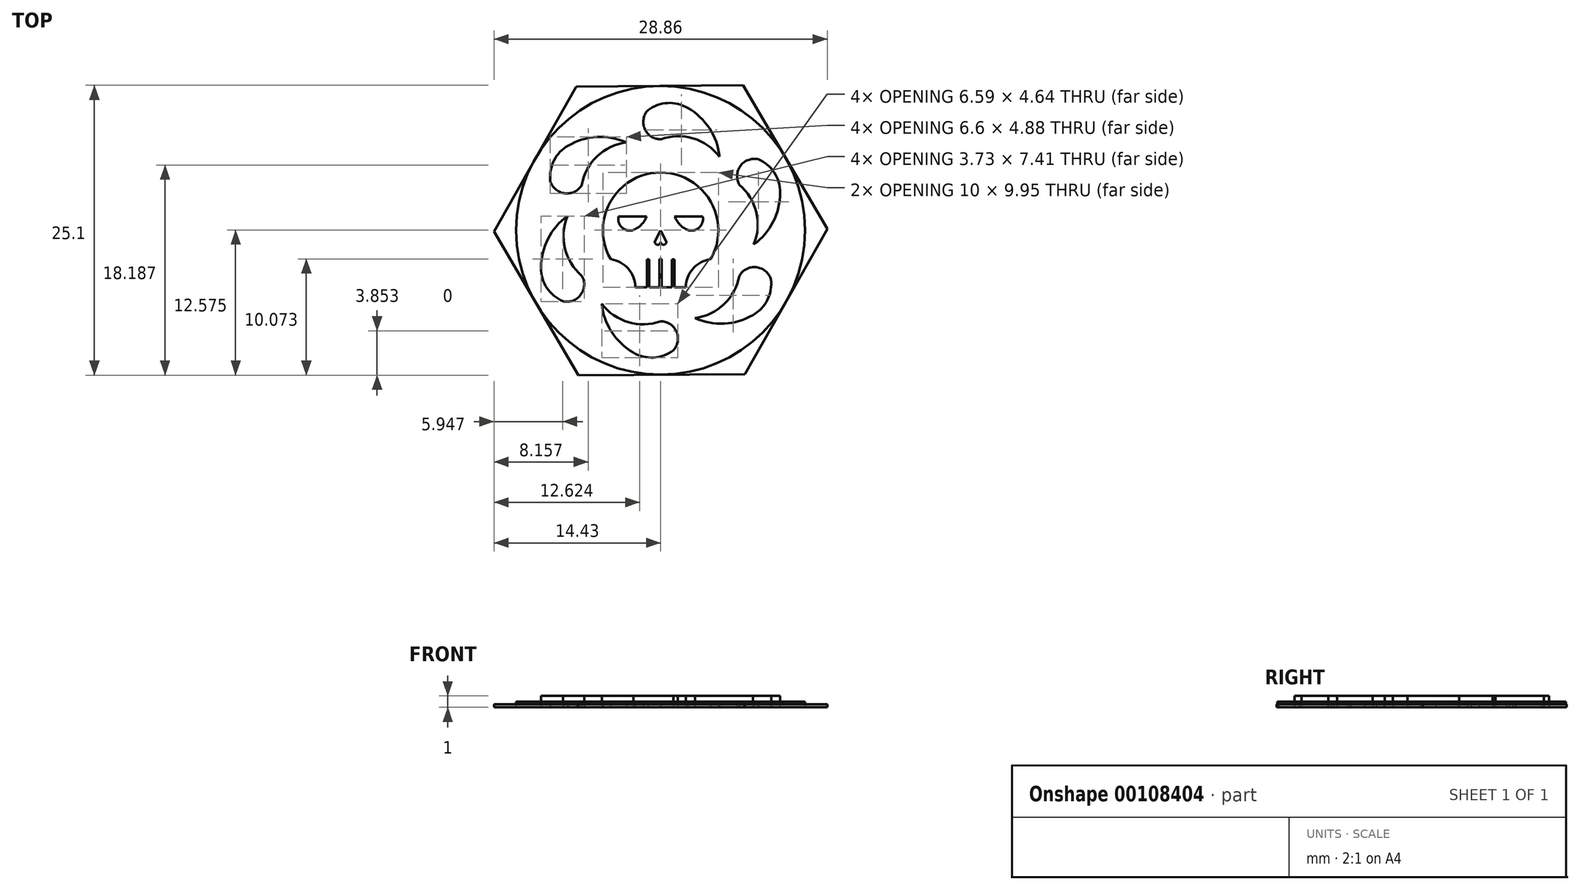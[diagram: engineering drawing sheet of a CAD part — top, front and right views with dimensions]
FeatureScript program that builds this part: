
annotation { "Feature Type Name" : "Feature", "Feature Type Description" : "" }
export const myFeature = defineFeature(function(context is Context, id is Id, definition is map)
    precondition{}
    {
        {
            var Q0;
            Q0=qCreatedBy(makeId("Top.planeOp"),FACE);
            var sketch = newSketch(context, id + "F0", { "sketchPlane" : qUnion([Q0])});
            skArc(sketch, "E0", {"start": v(4.33, -2.5) * mm, "mid": v(0, 5) * mm, "end": v(-4.33, -2.5) * mm});
            skLineSegment(sketch, "E1", {"start": v(0, -1) * mm, "end": v(0, -2.5) * mm});
            skArc(sketch, "E2", {"start": v(-2.19, -4.95) * mm, "mid": v(-2.8, -3.33) * mm, "end": v(-4.33, -2.5) * mm});
            skArc(sketch, "E3", {"start": v(4.33, -2.5) * mm, "mid": v(2.8, -3.33) * mm, "end": v(2.19, -4.95) * mm});
            skLineSegment(sketch, "E4", {"start": v(2.19, -4.95) * mm, "end": v(-2.19, -4.95) * mm});
            skPoint(sketch, "E5.start.orphan", {"position": v(0, -2.5) * mm});
            skLineSegment(sketch, "E6", {"start": v(0, 0) * mm, "end": v(0, 1.2) * mm});
            skLineSegment(sketch, "E7", {"start": v(-1.21, 1.2) * mm, "end": v(-3.64, 1.2) * mm});
            skLineSegment(sketch, "E8", {"start": v(1.21, 1.2) * mm, "end": v(3.64, 1.2) * mm});
            skLineSegment(sketch, "E9", {"start": v(-2.43, 1.2) * mm, "end": v(-3.64, 1.2) * mm});
            skLineSegment(sketch, "E10", {"start": v(-2.43, 1.2) * mm, "end": v(-1.21, 1.2) * mm});
            skLineSegment(sketch, "E11", {"start": v(1.21, 1.2) * mm, "end": v(2.43, 1.2) * mm});
            skLineSegment(sketch, "E12", {"start": v(2.43, 1.2) * mm, "end": v(3.64, 1.2) * mm});
            skArc(sketch, "E13", {"start": v(-3.64, 1.2) * mm, "mid": v(-3.37, 0.26) * mm, "end": v(-2.43, 0) * mm});
            skArc(sketch, "E14", {"start": v(-2.43, 0) * mm, "mid": v(-1.69, 0.46) * mm, "end": v(-1.21, 1.2) * mm});
            skArc(sketch, "E15", {"start": v(1.21, 1.2) * mm, "mid": v(1.69, 0.46) * mm, "end": v(2.43, 0) * mm});
            skArc(sketch, "E16", {"start": v(2.43, 0) * mm, "mid": v(3.37, 0.26) * mm, "end": v(3.64, 1.2) * mm});
            skPoint(sketch, "E17.orphan", {"position": v(-4.85, 1.2) * mm});
            skPoint(sketch, "E18.orphan", {"position": v(4.85, 1.2) * mm});
            skLineSegment(sketch, "E19", {"start": v(0, -1) * mm, "end": v(0, -1.5) * mm});
            skLineSegment(sketch, "E20", {"start": v(-0.5, -1) * mm, "end": v(0, 0) * mm});
            skLineSegment(sketch, "E21", {"start": v(0, 0) * mm, "end": v(0.5, -1) * mm});
            skArc(sketch, "E22", {"start": v(-0.5, -1) * mm, "mid": v(-0.25, -1.25) * mm, "end": v(0, -1) * mm});
            skArc(sketch, "E23", {"start": v(0, -1) * mm, "mid": v(0.25, -1.25) * mm, "end": v(0.5, -1) * mm});
            skPoint(sketch, "E23.midSnap0", {"position": v(0.25, -1) * mm});
            skPoint(sketch, "E23.midSnap1", {"position": v(0, -1.25) * mm});
            skLineSegment(sketch, "E24", {"start": v(0, -4.95) * mm, "end": v(-2.19, -4.95) * mm});
            skLineSegment(sketch, "E25", {"start": v(0, -4.95) * mm, "end": v(2.19, -4.95) * mm});
            skLineSegment(sketch, "E26", {"start": v(-0.1, -4.78) * mm, "end": v(-0.1, -4.95) * mm});
            skLineSegment(sketch, "E27", {"start": v(0.1, -4.78) * mm, "end": v(0.1, -4.95) * mm});
            skLineSegment(sketch, "E28", {"start": v(-1.2, -4.81) * mm, "end": v(-1.2, -4.95) * mm});
            skLineSegment(sketch, "E29", {"start": v(-1, -4.81) * mm, "end": v(-1, -4.95) * mm});
            skLineSegment(sketch, "E30", {"start": v(1, -4.81) * mm, "end": v(1, -4.95) * mm});
            skLineSegment(sketch, "E31", {"start": v(1.2, -4.81) * mm, "end": v(1.2, -4.95) * mm});
            skLineSegment(sketch, "E32", {"start": v(0.1, -4.78) * mm, "end": v(0.1, -2.5) * mm});
            skLineSegment(sketch, "E33", {"start": v(-0.1, -4.78) * mm, "end": v(-0.1, -2.5) * mm});
            skLineSegment(sketch, "E34", {"start": v(-1, -4.81) * mm, "end": v(-1, -2.53) * mm});
            skLineSegment(sketch, "E35", {"start": v(-1.2, -4.81) * mm, "end": v(-1.2, -2.53) * mm});
            skLineSegment(sketch, "E36", {"start": v(1, -4.81) * mm, "end": v(1, -2.53) * mm});
            skLineSegment(sketch, "E37", {"start": v(1.2, -4.81) * mm, "end": v(1.2, -2.53) * mm});
            skLineSegment(sketch, "E38", {"start": v(-1.2, -2.53) * mm, "end": v(-1, -2.53) * mm});
            skLineSegment(sketch, "E39", {"start": v(-0.1, -2.5) * mm, "end": v(0.1, -2.5) * mm});
            skLineSegment(sketch, "E40", {"start": v(1, -2.53) * mm, "end": v(1.2, -2.53) * mm});
            skCircle(sketch, "E41", {"center": v(0, 0) * mm, "radius": 12.5 * mm});
            skLineSegment(sketch, "E42", {"start": v(0, 0) * mm, "end": v(0, 12.5) * mm});
            skLineSegment(sketch, "E43", {"start": v(0, 6.25) * mm, "end": v(0, 12.5) * mm});
            skArc(sketch, "E44", {"start": v(5.1, 6.38) * mm, "mid": v(2.8, 7.96) * mm, "end": v(0, 7.87) * mm});
            skArc(sketch, "E45", {"start": v(2.35, 10.59) * mm, "mid": v(0.6, 11.02) * mm, "end": v(-1.1, 10.4) * mm});
            skArc(sketch, "E46.trimOffspring", {"start": v(-1.1, 10.4) * mm, "mid": v(-1.38, 8.78) * mm, "end": v(0, 7.87) * mm});
            skPoint(sketch, "E47.center.orphan", {"position": v(0, 9.38) * mm});
            skArc(sketch, "E48", {"start": v(5.1, 6.38) * mm, "mid": v(4.24, 8.81) * mm, "end": v(2.35, 10.59) * mm});
            skArc(sketch, "E49.1.0", {"start": v(-2.97, 7.6) * mm, "mid": v(-5.52, 8.08) * mm, "end": v(-8, 7.33) * mm});
            skArc(sketch, "E49.1.1", {"start": v(-8, 7.33) * mm, "mid": v(-9.24, 6.03) * mm, "end": v(-9.55, 4.25) * mm});
            skArc(sketch, "E49.1.2", {"start": v(-9.55, 4.25) * mm, "mid": v(-8.29, 3.2) * mm, "end": v(-6.82, 3.94) * mm});
            skArc(sketch, "E49.1.3", {"start": v(-2.97, 7.6) * mm, "mid": v(-5.5, 6.4) * mm, "end": v(-6.82, 3.94) * mm});
            skArc(sketch, "E49.2.0", {"start": v(-8.07, 1.23) * mm, "mid": v(-9.75, -0.74) * mm, "end": v(-10.35, -3.26) * mm});
            skArc(sketch, "E49.2.1", {"start": v(-10.35, -3.26) * mm, "mid": v(-9.84, -4.99) * mm, "end": v(-8.46, -6.15) * mm});
            skArc(sketch, "E49.2.2", {"start": v(-8.46, -6.15) * mm, "mid": v(-6.91, -5.58) * mm, "end": v(-6.82, -3.94) * mm});
            skArc(sketch, "E49.2.3", {"start": v(-8.07, 1.23) * mm, "mid": v(-8.29, -1.56) * mm, "end": v(-6.82, -3.94) * mm});
            skArc(sketch, "E49.3.0", {"start": v(-5.1, -6.38) * mm, "mid": v(-4.24, -8.81) * mm, "end": v(-2.35, -10.59) * mm});
            skArc(sketch, "E49.3.1", {"start": v(-2.35, -10.59) * mm, "mid": v(-0.6, -11.02) * mm, "end": v(1.1, -10.4) * mm});
            skArc(sketch, "E49.3.2", {"start": v(1.1, -10.4) * mm, "mid": v(1.38, -8.78) * mm, "end": v(0, -7.87) * mm});
            skArc(sketch, "E49.3.3", {"start": v(-5.1, -6.38) * mm, "mid": v(-2.8, -7.96) * mm, "end": v(0, -7.87) * mm});
            skArc(sketch, "E49.4.0", {"start": v(2.97, -7.6) * mm, "mid": v(5.52, -8.08) * mm, "end": v(8, -7.33) * mm});
            skArc(sketch, "E49.4.1", {"start": v(8, -7.33) * mm, "mid": v(9.24, -6.03) * mm, "end": v(9.55, -4.25) * mm});
            skArc(sketch, "E49.4.2", {"start": v(9.55, -4.25) * mm, "mid": v(8.29, -3.2) * mm, "end": v(6.82, -3.94) * mm});
            skArc(sketch, "E49.4.3", {"start": v(2.97, -7.6) * mm, "mid": v(5.5, -6.4) * mm, "end": v(6.82, -3.94) * mm});
            skArc(sketch, "E49.5.0", {"start": v(8.07, -1.23) * mm, "mid": v(9.75, 0.74) * mm, "end": v(10.35, 3.26) * mm});
            skArc(sketch, "E49.5.1", {"start": v(10.35, 3.26) * mm, "mid": v(9.84, 4.99) * mm, "end": v(8.46, 6.15) * mm});
            skArc(sketch, "E49.5.2", {"start": v(8.46, 6.15) * mm, "mid": v(6.91, 5.58) * mm, "end": v(6.82, 3.94) * mm});
            skArc(sketch, "E49.5.3", {"start": v(8.07, -1.23) * mm, "mid": v(8.29, 1.56) * mm, "end": v(6.82, 3.94) * mm});
            skCircle(sketch, "E50.cCircle", {"center": v(0, 0) * mm, "radius": 12.5 * mm, "construction": true});
            skLineSegment(sketch, "E50.0", {"start": v(-14.43, -0.1) * mm, "end": v(-7.3, 12.45) * mm});
            skLineSegment(sketch, "E50.1", {"start": v(-7.3, 12.45) * mm, "end": v(7.13, 12.55) * mm});
            skLineSegment(sketch, "E50.2", {"start": v(7.13, 12.55) * mm, "end": v(14.43, 0.1) * mm});
            skLineSegment(sketch, "E50.3", {"start": v(14.43, 0.1) * mm, "end": v(7.3, -12.45) * mm});
            skLineSegment(sketch, "E50.4", {"start": v(7.3, -12.45) * mm, "end": v(-7.13, -12.55) * mm});
            skLineSegment(sketch, "E50.5", {"start": v(-7.13, -12.55) * mm, "end": v(-14.43, -0.1) * mm});
            skPoint(sketch, "E50.0.midPoint", {"position": v(-10.87, 6.17) * mm});
            skSolve(sketch);
        }
        {
            var Q0;
            {var subQ0=sQuery(id+"F0.wireOp",EDGE,"E44");Q0=makeQuery(id+"F0.imprint","IMPRINT",FACE,{"disambiguationData":[TD([[makeQuery(id+"F0.imprint","IMPRINT",EDGE,{"derivedFrom":subQ0}),-1.0]])]});}
            var Q1;
            {var subQ0=sQuery(id+"F0.wireOp",EDGE,"E46.trimOffspring");Q1=makeQuery(id+"F0.imprint","IMPRINT",FACE,{"disambiguationData":[TD([[makeQuery(id+"F0.imprint","IMPRINT",EDGE,{"derivedFrom":subQ0}),1.0]])]});}
            var Q2;
            Q2=makeQuery(id+"F0.imprint","IMPRINT",FACE,{"disambiguationData":[TD([[makeQuery(id+"F0.imprint","IMPRINT",EDGE,{"derivedFrom":sQuery(id+"F0.wireOp",EDGE,"E49.1.0")}),1.0]])]});
            var Q3;
            Q3=makeQuery(id+"F0.imprint","IMPRINT",FACE,{"disambiguationData":[TD([[makeQuery(id+"F0.imprint","IMPRINT",EDGE,{"derivedFrom":sQuery(id+"F0.wireOp",EDGE,"E49.2.0")}),1.0]])]});
            var Q4;
            Q4=makeQuery(id+"F0.imprint","IMPRINT",FACE,{"disambiguationData":[TD([[makeQuery(id+"F0.imprint","IMPRINT",EDGE,{"derivedFrom":sQuery(id+"F0.wireOp",EDGE,"E49.3.0")}),1.0]])]});
            var Q5;
            Q5=makeQuery(id+"F0.imprint","IMPRINT",FACE,{"disambiguationData":[TD([[makeQuery(id+"F0.imprint","IMPRINT",EDGE,{"derivedFrom":sQuery(id+"F0.wireOp",EDGE,"E49.4.0")}),1.0]])]});
            var Q6;
            Q6=makeQuery(id+"F0.imprint","IMPRINT",FACE,{"disambiguationData":[TD([[makeQuery(id+"F0.imprint","IMPRINT",EDGE,{"derivedFrom":sQuery(id+"F0.wireOp",EDGE,"E49.5.0")}),1.0]])]});
            var Q7;
            {var subQ6=sQuery(id+"F0.wireOp",EDGE,"E1");Q7=makeQuery(id+"F0.imprint","IMPRINT",FACE,{"disambiguationData":[TD([[makeQuery(id+"F0.imprint","IMPRINT",EDGE,{"derivedFrom":subQ6}),1.0]])]});}
            var Q8;
            {var subQ7=sQuery(id+"F0.wireOp",EDGE,"E1");Q8=makeQuery(id+"F0.imprint","IMPRINT",FACE,{"disambiguationData":[TD([[makeQuery(id+"F0.imprint","IMPRINT",EDGE,{"derivedFrom":subQ7}),-1.0]])]});}
            extrude(context, id + "F1", {"entities" : qUnion([Q0, Q1, Q2, Q3, Q4, Q5, Q6, Q7, Q8]), "depth" : 1 * mm});
        }
        {
            var Q0;
            {var subQ8=sQuery(id+"F0.wireOp",EDGE,"E2");Q0=makeQuery(id+"F0.imprint","IMPRINT",FACE,{"disambiguationData":[TD([[makeQuery(id+"F0.imprint","IMPRINT",EDGE,{"derivedFrom":subQ8}),1.0]])]});}
            var Q1;
            Q1=makeQuery(id+"F0.imprint","IMPRINT",FACE,{"disambiguationData":[TD([[makeQuery(id+"F0.imprint","IMPRINT",EDGE,{"derivedFrom":sQuery(id+"F0.wireOp",EDGE,"E9")}),1.0]])]});
            var Q2;
            Q2=makeQuery(id+"F0.imprint","IMPRINT",FACE,{"disambiguationData":[TD([[makeQuery(id+"F0.imprint","IMPRINT",EDGE,{"derivedFrom":sQuery(id+"F0.wireOp",EDGE,"E11")}),-1.0]])]});
            var Q3;
            Q3=makeQuery(id+"F0.imprint","IMPRINT",FACE,{"disambiguationData":[TD([[makeQuery(id+"F0.imprint","IMPRINT",EDGE,{"derivedFrom":sQuery(id+"F0.wireOp",EDGE,"E20")}),-1.0]])]});
            var Q4;
            {var subQ1=sQuery(id+"F0.wireOp",EDGE,"E28");Q4=makeQuery(id+"F0.imprint","IMPRINT",FACE,{"disambiguationData":[TD([[makeQuery(id+"F0.imprint","IMPRINT",EDGE,{"derivedFrom":subQ1}),1.0]])]});}
            var Q5;
            {var subQ1=sQuery(id+"F0.wireOp",EDGE,"E26");Q5=makeQuery(id+"F0.imprint","IMPRINT",FACE,{"disambiguationData":[TD([[makeQuery(id+"F0.imprint","IMPRINT",EDGE,{"derivedFrom":subQ1}),1.0]])]});}
            var Q6;
            {var subQ1=sQuery(id+"F0.wireOp",EDGE,"E30");Q6=makeQuery(id+"F0.imprint","IMPRINT",FACE,{"disambiguationData":[TD([[makeQuery(id+"F0.imprint","IMPRINT",EDGE,{"derivedFrom":subQ1}),1.0]])]});}
            extrude(context, id + "F2", {"entities" : qUnion([Q0, Q1, Q2, Q3, Q4, Q5, Q6]), "depth" : .5 * mm});
        }
        {
            var Q0;
            {var subQ0=sQuery(id+"F0.wireOp",EDGE,"E41");var subQ1=makeQuery(id+"F0.imprint","IMPRINT",VERTEX,{"derivedFrom":subQ0});Q0=makeQuery(id+"F0.imprint","IMPRINT",FACE,{"disambiguationData":[TD([[makeQuery(id+"F0.imprint","IMPRINT",EDGE,{"disambiguationData":[TD([[subQ1,1.0]])],"derivedFrom":subQ0}),-1.0]])]});}
            var Q1;
            {var subQ0=sQuery(id+"F0.wireOp",EDGE,"E50.1");var subQ1=sQuery(id+"F0.wireOp",EDGE,"E41");var subQ2=makeQuery(id+"F0.imprint","INTERSECT",VERTEX,{"derivedFrom":[subQ1,subQ0]});Q1=makeQuery(id+"F0.imprint","IMPRINT",FACE,{"disambiguationData":[TD([[makeQuery(id+"F0.imprint","IMPRINT",EDGE,{"disambiguationData":[TD([[subQ2,-1.0]])],"derivedFrom":subQ1}),-1.0]])]});}
            var Q2;
            {var subQ0=sQuery(id+"F0.wireOp",EDGE,"E50.5");var subQ1=sQuery(id+"F0.wireOp",EDGE,"E41");var subQ2=makeQuery(id+"F0.imprint","INTERSECT",VERTEX,{"derivedFrom":[subQ1,subQ0]});Q2=makeQuery(id+"F0.imprint","IMPRINT",FACE,{"disambiguationData":[TD([[makeQuery(id+"F0.imprint","IMPRINT",EDGE,{"disambiguationData":[TD([[subQ2,-1.0]])],"derivedFrom":subQ1}),-1.0]])]});}
            var Q3;
            {var subQ0=sQuery(id+"F0.wireOp",EDGE,"E50.4");var subQ1=sQuery(id+"F0.wireOp",EDGE,"E41");var subQ2=makeQuery(id+"F0.imprint","INTERSECT",VERTEX,{"derivedFrom":[subQ1,subQ0]});Q3=makeQuery(id+"F0.imprint","IMPRINT",FACE,{"disambiguationData":[TD([[makeQuery(id+"F0.imprint","IMPRINT",EDGE,{"disambiguationData":[TD([[subQ2,-1.0]])],"derivedFrom":subQ1}),-1.0]])]});}
            var Q4;
            {var subQ0=sQuery(id+"F0.wireOp",EDGE,"E50.2");var subQ1=sQuery(id+"F0.wireOp",EDGE,"E41");var subQ2=makeQuery(id+"F0.imprint","INTERSECT",VERTEX,{"derivedFrom":[subQ1,subQ0]});Q4=makeQuery(id+"F0.imprint","IMPRINT",FACE,{"disambiguationData":[TD([[makeQuery(id+"F0.imprint","IMPRINT",EDGE,{"disambiguationData":[TD([[subQ2,1.0]])],"derivedFrom":subQ1}),-1.0]])]});}
            var Q5;
            {var subQ15=sQuery(id+"F0.wireOp",EDGE,"E2");Q5=makeQuery(id+"F0.imprint","IMPRINT",FACE,{"disambiguationData":[TD([[makeQuery(id+"F0.imprint","IMPRINT",EDGE,{"derivedFrom":subQ15}),1.0]])]});}
            var Q6;
            {var subQ0=sQuery(id+"F0.wireOp",EDGE,"E50.0");var subQ1=sQuery(id+"F0.wireOp",EDGE,"E41");var subQ2=makeQuery(id+"F0.imprint","INTERSECT",VERTEX,{"derivedFrom":[subQ1,subQ0]});Q6=makeQuery(id+"F0.imprint","IMPRINT",FACE,{"disambiguationData":[TD([[makeQuery(id+"F0.imprint","IMPRINT",EDGE,{"disambiguationData":[TD([[subQ2,-1.0]])],"derivedFrom":subQ1}),-1.0]])]});}
            extrude(context, id + "F3", {"entities" : qUnion([Q0, Q1, Q2, Q3, Q4, Q5, Q6]), "depth" : .25 * mm});
        }
    });
